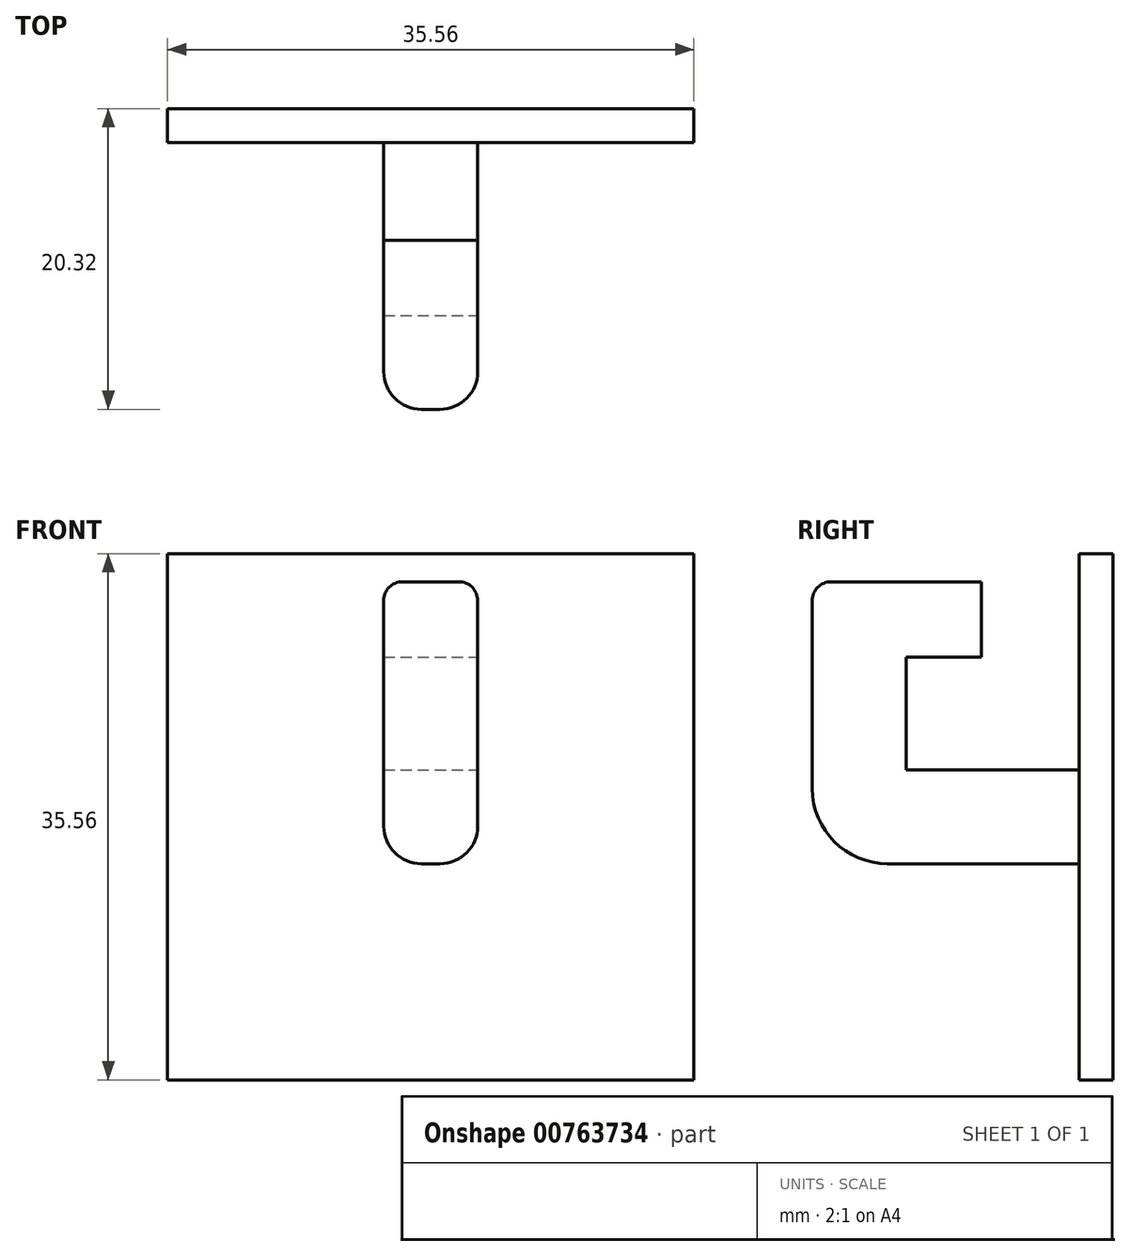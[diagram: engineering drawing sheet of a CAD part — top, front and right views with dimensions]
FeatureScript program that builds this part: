
annotation { "Feature Type Name" : "Feature", "Feature Type Description" : "" }
export const myFeature = defineFeature(function(context is Context, id is Id, definition is map)
    precondition{}
    {
        {
            var Q0;
            Q0=qCreatedBy(makeId("Front.planeOp"),FACE);
            var sketch = newSketch(context, id + "F0", { "sketchPlane" : qUnion([Q0])});
            skLineSegment(sketch, "E0.bottom", {"start": v(-17.78, 17.78) * mm, "end": v(17.78, 17.78) * mm});
            skLineSegment(sketch, "E0.top", {"start": v(-17.78, -17.78) * mm, "end": v(17.78, -17.78) * mm});
            skLineSegment(sketch, "E0.left", {"start": v(-17.78, 17.78) * mm, "end": v(-17.78, -17.78) * mm});
            skLineSegment(sketch, "E0.right", {"start": v(17.78, 17.78) * mm, "end": v(17.78, -17.78) * mm});
            skPoint(sketch, "E0.middle", {"position": v(0, 0) * mm});
            skLineSegment(sketch, "E1.bottom", {"start": v(-3.17, 3.18) * mm, "end": v(3.18, 3.18) * mm});
            skLineSegment(sketch, "E1.top", {"start": v(-3.18, -3.18) * mm, "end": v(3.18, -3.18) * mm});
            skLineSegment(sketch, "E1.left", {"start": v(-3.18, 3.18) * mm, "end": v(-3.18, -3.18) * mm});
            skLineSegment(sketch, "E1.right", {"start": v(3.18, 3.18) * mm, "end": v(3.18, -3.18) * mm});
            skSolve(sketch);
        }
        {
            var Q0;
            Q0 = qSketchRegion(id + "F0", true);
            extrude(context, id + "F1", {"entities" : qUnion([Q0]), "depth" : 2.3 * mm, "offsetDistance" : 25.4 * mm});
        }
        {
            var Q0;
            Q0=makeQuery(id+"F0.imprint","IMPRINT",FACE,{"disambiguationData":[TD([[makeQuery(id+"F0.imprint","IMPRINT",EDGE,{"derivedFrom":sQuery(id+"F0.wireOp",EDGE,"E1.bottom")}),-1.0]])]});
            extrude(context, id + "F2", {"entities" : qUnion([Q0]), "operationType" : NewBodyOperationType.ADD, "depth" : 20.32 * mm, "offsetDistance" : 25.4 * mm});
        }
        {
            var Q0;
            Q0=makeQuery(id+"F2.opExtrude","SWEPT_FACE",FACE,{"disambiguationData":[OSD([sQuery(id+"F0.wireOp",EDGE,"E1.bottom")])]});
            var sketch = newSketch(context, id + "F3", { "sketchPlane" : qUnion([Q0])});
            skLineSegment(sketch, "E2.bottom", {"start": v(-3.17, -13.97) * mm, "end": v(3.18, -13.97) * mm});
            skLineSegment(sketch, "E2.top", {"start": v(-3.17, -20.32) * mm, "end": v(3.18, -20.32) * mm});
            skLineSegment(sketch, "E2.left", {"start": v(-3.18, -13.97) * mm, "end": v(-3.17, -20.32) * mm});
            skLineSegment(sketch, "E2.right", {"start": v(3.18, -13.97) * mm, "end": v(3.18, -20.32) * mm});
            skSolve(sketch);
        }
        {
            var Q0;
            Q0 = qSketchRegion(id + "F3", true);
            extrude(context, id + "F4", {"entities" : qUnion([Q0]), "operationType" : NewBodyOperationType.ADD, "depth" : 12.7 * mm, "offsetDistance" : 25.4 * mm});
        }
        {
            var Q0;
            Q0=makeQuery(id+"F2.opExtrude","CAP_EDGE",EDGE,{"disambiguationData":[OSD([sQuery(id+"F0.wireOp",EDGE,"E1.top")])],"isStart":false});
            fillet(context, id + "F5", {"entities" : qUnion([Q0]), "radius" : 5.08 * mm, "tangentPropagation" : true, "allowEdgeOverflow" : false});
        }
        {
            var Q0;
            Q0=makeQuery(id+"F4.boolean.opBoolean","MERGE",EDGE,{"derivedFrom":[makeQuery(id+"F2.opExtrude","CAP_EDGE",EDGE,{"disambiguationData":[OSD([sQuery(id+"F0.wireOp",EDGE,"E1.right")])],"isStart":false}),makeQuery(id+"F4.opExtrude","SWEPT_EDGE",EDGE,{"disambiguationData":[OSD([sQuery(id+"F3.wireOp",EDGE,"E2.top"),sQuery(id+"F3.wireOp",EDGE,"E2.right")])]})]});
            var Q1;
            Q1=makeQuery(id+"F4.boolean.opBoolean","MERGE",EDGE,{"derivedFrom":[makeQuery(id+"F2.opExtrude","CAP_EDGE",EDGE,{"disambiguationData":[OSD([sQuery(id+"F0.wireOp",EDGE,"E1.left")])],"isStart":false}),makeQuery(id+"F4.opExtrude","SWEPT_EDGE",EDGE,{"disambiguationData":[OSD([sQuery(id+"F3.wireOp",EDGE,"E2.top"),sQuery(id+"F3.wireOp",EDGE,"E2.left")])]})]});
            fillet(context, id + "F6", {"entities" : qUnion([Q0, Q1]), "radius" : 2.54 * mm, "tangentPropagation" : true, "allowEdgeOverflow" : false});
        }
        {
            var Q0;
            Q0=makeQuery(id+"F4.opExtrude","SWEPT_FACE",FACE,{"disambiguationData":[OSD([sQuery(id+"F3.wireOp",EDGE,"E2.bottom")])]});
            var sketch = newSketch(context, id + "F7", { "sketchPlane" : qUnion([Q0])});
            skLineSegment(sketch, "E3.bottom", {"start": v(3.17, 15.88) * mm, "end": v(-3.18, 15.88) * mm});
            skLineSegment(sketch, "E3.top", {"start": v(3.18, 10.8) * mm, "end": v(-3.18, 10.8) * mm});
            skLineSegment(sketch, "E3.left", {"start": v(3.18, 15.88) * mm, "end": v(3.18, 10.8) * mm});
            skLineSegment(sketch, "E3.right", {"start": v(-3.18, 15.88) * mm, "end": v(-3.18, 10.8) * mm});
            skSolve(sketch);
        }
        {
            var Q0;
            Q0 = qSketchRegion(id + "F7", true);
            extrude(context, id + "F8", {"entities" : qUnion([Q0]), "operationType" : NewBodyOperationType.ADD, "depth" : 5.08 * mm, "offsetDistance" : 25.4 * mm});
        }
        {
            var Q0;
            {var subQ0=sQuery(id+"F3.wireOp",EDGE,"E2.right");var subQ1=sQuery(id+"F3.wireOp",EDGE,"E2.top");Q0=makeQuery(id+"F6.opFillet","BLEND_EDGE",EDGE,{"blendedFrom":[makeQuery(id+"F4.boolean.opBoolean","MERGE",EDGE,{"derivedFrom":[makeQuery(id+"F2.opExtrude","CAP_EDGE",EDGE,{"disambiguationData":[OSD([sQuery(id+"F0.wireOp",EDGE,"E1.right")])],"isStart":false}),makeQuery(id+"F4.opExtrude","SWEPT_EDGE",EDGE,{"disambiguationData":[OSD([subQ1,subQ0])]})]}),makeQuery(id+"F4.opExtrude","CAP_FACE",FACE,{"disambiguationData":[OSD([sQuery(id+"F3.wireOp",EDGE,"E2.bottom"),subQ1,sQuery(id+"F3.wireOp",EDGE,"E2.left"),subQ0])],"isStart":false})],"blendedInto":[makeQuery(id+"F4.opExtrude","CAP_FACE",FACE,{"disambiguationData":[OSD([sQuery(id+"F3.wireOp",EDGE,"E2.bottom"),subQ1,sQuery(id+"F3.wireOp",EDGE,"E2.left"),subQ0])],"isStart":false})]});}
            var Q1;
            Q1=makeQuery(id+"F4.opExtrude","CAP_EDGE",EDGE,{"disambiguationData":[OSD([sQuery(id+"F3.wireOp",EDGE,"E2.top")])],"isStart":false});
            var Q2;
            {var subQ0=sQuery(id+"F3.wireOp",EDGE,"E2.left");var subQ1=sQuery(id+"F3.wireOp",EDGE,"E2.top");Q2=makeQuery(id+"F6.opFillet","BLEND_EDGE",EDGE,{"blendedFrom":[makeQuery(id+"F4.boolean.opBoolean","MERGE",EDGE,{"derivedFrom":[makeQuery(id+"F2.opExtrude","CAP_EDGE",EDGE,{"disambiguationData":[OSD([sQuery(id+"F0.wireOp",EDGE,"E1.left")])],"isStart":false}),makeQuery(id+"F4.opExtrude","SWEPT_EDGE",EDGE,{"disambiguationData":[OSD([subQ1,subQ0])]})]}),makeQuery(id+"F4.opExtrude","CAP_FACE",FACE,{"disambiguationData":[OSD([sQuery(id+"F3.wireOp",EDGE,"E2.bottom"),subQ1,subQ0,sQuery(id+"F3.wireOp",EDGE,"E2.right")])],"isStart":false})],"blendedInto":[makeQuery(id+"F4.opExtrude","CAP_FACE",FACE,{"disambiguationData":[OSD([sQuery(id+"F3.wireOp",EDGE,"E2.bottom"),subQ1,subQ0,sQuery(id+"F3.wireOp",EDGE,"E2.right")])],"isStart":false})]});}
            fillet(context, id + "F9", {"entities" : qUnion([Q0, Q1, Q2]), "radius" : 1.27 * mm, "tangentPropagation" : true, "allowEdgeOverflow" : false});
        }
    });
